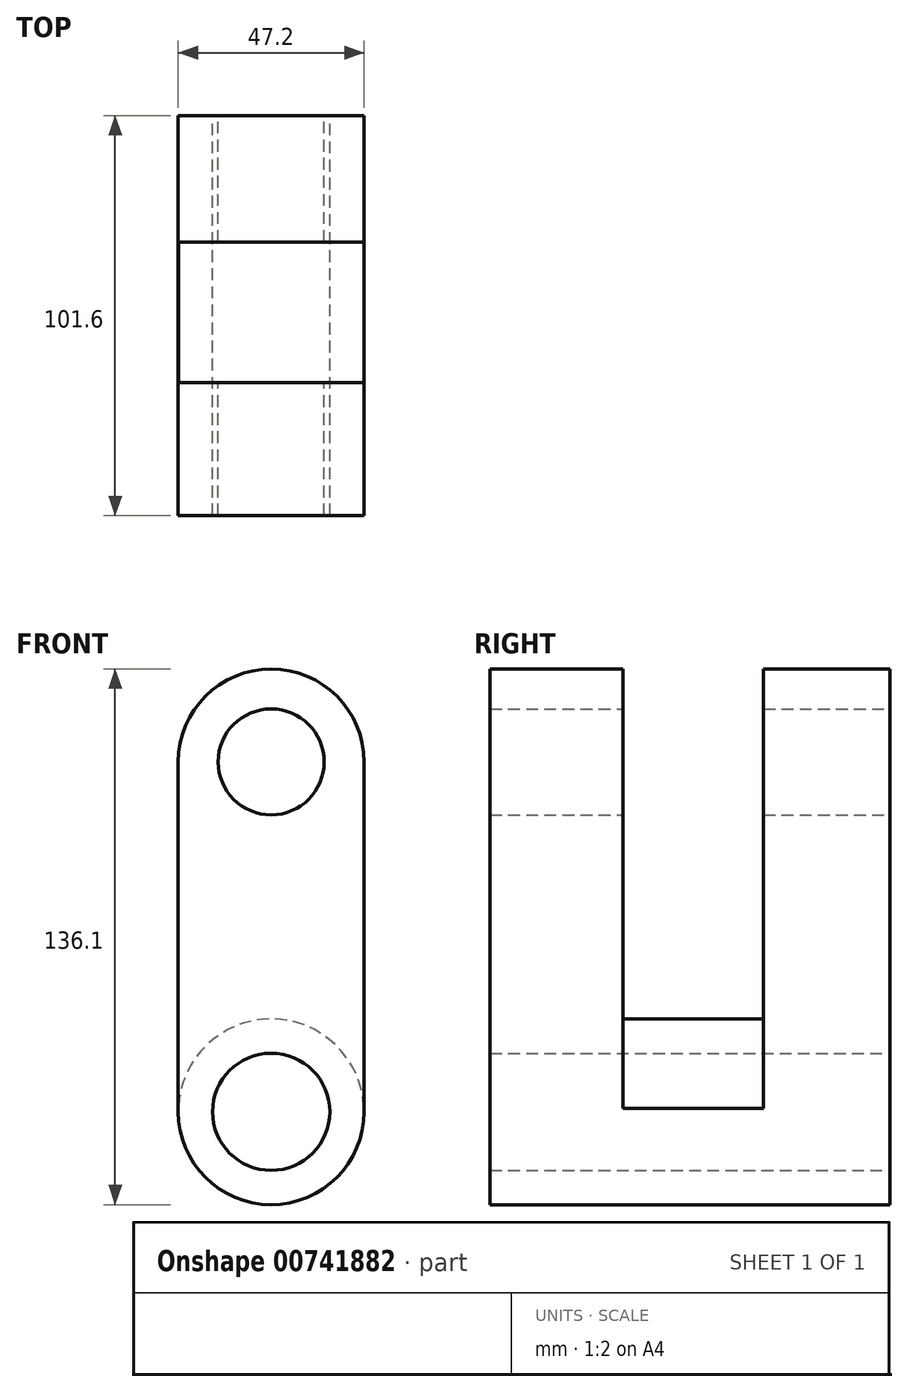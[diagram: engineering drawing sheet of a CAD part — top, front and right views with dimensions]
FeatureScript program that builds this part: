
annotation { "Feature Type Name" : "Feature", "Feature Type Description" : "" }
export const myFeature = defineFeature(function(context is Context, id is Id, definition is map)
    precondition{}
    {
        {
            var Q0;
            Q0=qCreatedBy(makeId("Front.planeOp"),FACE);
            var sketch = newSketch(context, id + "F0", { "sketchPlane" : qUnion([Q0])});
            skLineSegment(sketch, "E0.bottom", {"start": v(23.6, 44.45) * mm, "end": v(-23.6, 44.45) * mm});
            skLineSegment(sketch, "E0.top", {"start": v(23.6, -44.45) * mm, "end": v(-23.6, -44.45) * mm});
            skLineSegment(sketch, "E0.left", {"start": v(23.6, 44.45) * mm, "end": v(23.6, -44.45) * mm});
            skLineSegment(sketch, "E0.right", {"start": v(-23.6, 44.45) * mm, "end": v(-23.6, -44.45) * mm});
            skPoint(sketch, "E0.middle", {"position": v(0, 0) * mm});
            skCircle(sketch, "E1", {"center": v(0, 44.45) * mm, "radius": 23.6 * mm});
            skCircle(sketch, "E2", {"center": v(0, -44.45) * mm, "radius": 23.6 * mm});
            skCircle(sketch, "E3", {"center": v(0, 44.45) * mm, "radius": 13.46 * mm});
            skCircle(sketch, "E4", {"center": v(0, -44.45) * mm, "radius": 14.9 * mm});
            skSolve(sketch);
        }
        {
            var Q0;
            Q0 = qSketchRegion(id + "F0", true);
            extrude(context, id + "F1", {"entities" : qUnion([Q0]), "depth" : 50.8 * mm, "offsetDistance" : 25.4 * mm, "hasSecondDirection" : true, "secondDirectionOppositeDirection" : true, "secondDirectionDepth" : 50.8 * mm});
        }
        {
            var Q0;
            {var subQ2=sQuery(id+"F0.wireOp",EDGE,"E0.right");Q0=makeQuery(id+"FPFXpqTyEhgpJVw_1.boolean.opBoolean","SPLIT",FACE,{"disambiguationData":[TD([makeQuery(id+"FPFXpqTyEhgpJVw_1.opExtrude","SWEPT_FACE",FACE,{"disambiguationData":[OSD([sQuery(id+"Fd22xvbS1O0wuHs_1.wireOp",EDGE,"66057513-d0ee-454d-9fb3-1772d3b7e8af.right")])]})])],"derivedFrom":makeQuery(id+"F1.opExtrude","SWEPT_FACE",FACE,{"disambiguationData":[OSD([subQ2])]})});}
            var sketch = newSketch(context, id + "F2", { "sketchPlane" : qUnion([Q0])});
            skLineSegment(sketch, "E5.bottom", {"start": v(0, -43.63) * mm, "end": v(16.99, -43.63) * mm});
            skLineSegment(sketch, "E5.top", {"start": v(0, 76.53) * mm, "end": v(16.99, 76.53) * mm});
            skLineSegment(sketch, "E5.left", {"start": v(0, -43.63) * mm, "end": v(0, 76.53) * mm});
            skLineSegment(sketch, "E5.right", {"start": v(16.99, -43.63) * mm, "end": v(16.99, 76.53) * mm});
            skLineSegment(sketch, "E6.bottom", {"start": v(0, -43.63) * mm, "end": v(-18.7, -43.63) * mm});
            skLineSegment(sketch, "E6.top", {"start": v(0, 76.46) * mm, "end": v(-18.7, 76.46) * mm});
            skLineSegment(sketch, "E6.left", {"start": v(0, -43.63) * mm, "end": v(0, 76.46) * mm});
            skLineSegment(sketch, "E6.right", {"start": v(-18.7, -43.63) * mm, "end": v(-18.7, 76.46) * mm});
            skSolve(sketch);
        }
        {
            var Q0;
            Q0 = qSketchRegion(id + "F2", true);
            extrude(context, id + "F3", {"entities" : qUnion([Q0]), "operationType" : NewBodyOperationType.REMOVE, "oppositeDirection" : true, "depth" : 152.4 * mm, "offsetDistance" : 25.4 * mm, "hasSecondDirection" : true, "secondDirectionOppositeDirection" : false, "secondDirectionDepth" : 152.4 * mm});
        }
        {
            var Q0;
            {var subQ1=sQuery(id+"F0.wireOp",EDGE,"E0.top");var subQ3=sQuery(id+"F0.wireOp",EDGE,"E4");var subQ4=makeQuery(id+"F0.imprint","INTERSECT",VERTEX,{"disambiguationData":[OD(0.0)],"derivedFrom":[subQ1,subQ3]});Q0=makeQuery(id+"F0.imprint","IMPRINT",FACE,{"disambiguationData":[TD([[makeQuery(id+"F0.imprint","IMPRINT",EDGE,{"disambiguationData":[TD([[subQ4,-1.0]])],"derivedFrom":subQ3}),-1.0]])]});}
            extrude(context, id + "F4", {"entities" : qUnion([Q0]), "operationType" : NewBodyOperationType.ADD, "depth" : 25.4 * mm, "offsetDistance" : 25.4 * mm, "hasSecondDirection" : true, "secondDirectionOppositeDirection" : true, "secondDirectionDepth" : 25.4 * mm});
        }
    });
